# Revit family: IEK_R19_L2(2)_Шкаф_ЩМПп_IP66_TETRA_Навесной
name_source: partatom
category: Электрооборудование
units: mm (PartAtom-declared; Revit-internal decimal feet)

## family parameters
Всегда вертикально = Да
На основе рабочей плоскости = Нет
Общий = Нет
При загрузке вырезать с полостями = Нет
Размер круглого соединителя = Использовать диаметр
Тип детали = Силовой щит
Точка расчета площади = Да

## types (20) — shared parameters
ADSK_Версия Revit = 2019
ADSK_Версия семейства = v1.0 2023-02-20
ADSK_Группирование = Продукция НКУ
ADSK_Единица измерения = шт
ADSK_Завод-изготовитель = IEK
ADSK_Количество = 1
mS_Guid = 821c7fcf-6e20-4866-bf76-5fe537ee1ddb
Группировать в спецификации = Нет
Инженерная_сеть = Нет
Серия = TETRA
zero-valued in all types: mS_Координация оборудования

## per-type parameters (varying)
| type | ADSK_Код изделия | ADSK_Марка | ADSK_Масса | ADSK_Наименование | ADSK_Обозначение | ADSK_Размер_Высота | ADSK_Размер_Глубина | ADSK_Размер_Ширина |
| TETRA_ЩМПп_(310x210x140)_Пластик_Навесной_ПрозрДверь | TR5-11-N-030-20-13-65 | ЩМПп-310-210-140_IP66 | 1.31 | TETRA 5 Корпус пластик. ЩМПп 300х200х130мм прозр. IP66 IEK | ЩМПп-310-210-140_IP66 | 310 мм | 140 мм | 210 мм |
| TETRA_ЩМПп_(360x260x160)_Пластик_Навесной_ПрозрДверь | TR5-11-N-035-25-15-65 | ЩМПп-360-260-160_IP66 | 1.92 | TETRA 5 Корпус пластик. ЩМПп 350х250х150мм прозр. IP66 IEK | ЩМПп-360-260-160_IP66 | 360 мм | 160 мм | 260 мм |
| TETRA_ЩМПп_(410x310x180)_Пластик_Навесной_ПрозрДверь | TR5-11-N-040-30-17-65 | ЩМПп-410-310-180_IP66 | 3.373 | TETRA 5 Корпус пластик. ЩМПп 400х300х170мм прозр. IP66 IEK | ЩМПп-410-310-180_IP66 | 410 мм | 180 мм | 310 мм |
| TETRA_ЩМПп_(410x310x230)_Пластик_Навесной_ПрозрДверь | TR5-11-N-040-30-22-65 | ЩМПп-410-310-230_IP66 | 2.92 | TETRA 5 Корпус пластик. ЩМПп 400х300х220мм прозр. IP66 IEK | ЩМПп-410-310-230_IP66 | 410 мм | 230 мм | 310 мм |
| TETRA_ЩМПп_(510x360x200)_Пластик_Навесной_ПрозрДверь | TR5-11-N-050-35-19-65 | ЩМПп-510-360-200_IP66 | 3.9 | TETRA 5 Корпус пластик. ЩМПп 500х350х190мм прозр. IP66 IEK | ЩМПп-510-360-200_IP66 | 510 мм | 200 мм | 360 мм |
| TETRA_ЩМПп_(510x410x190)_Пластик_Навесной_ПрозрДверь | TR5-11-N-050-40-18-65 | ЩМПп-510-410-190_IP66 | 4.17 | TETRA 5 Корпус пластик. ЩМПп 500х400х180мм прозр. IP66 IEK | ЩМПп-510-410-190_IP66 | 510 мм | 190 мм | 410 мм |
| TETRA_ЩМПп_(510x410x250)_Пластик_Навесной_ПрозрДверь | TR5-11-N-050-40-24-65 | ЩМПп-510-410-250_IP66 | 4.77 | TETRA 5 Корпус пластик. ЩМПп 500х400х240мм прозр. IP66 IEK | ЩМПп-510-410-250_IP66 | 510 мм | 250 мм | 410 мм |
| TETRA_ЩМПп_(610x410x210)_Пластик_Навесной_ПрозрДверь | TR5-11-N-060-40-20-65 | ЩМПп-610-410-210_IP66 | 5.43 | TETRA 5 Корпус пластик. ЩМПп 600х400х200мм прозр. IP66 IEK | ЩМПп-610-410-210_IP66 | 610 мм | 210 мм | 410 мм |
| TETRA_ЩМПп_(710x510x260)_Пластик_Навесной_ПрозрДверь | TR5-11-N-070-50-25-65 | ЩМПп-710-510-260_IP66 | 8.1 | TETRA 5 Корпус пластик. ЩМПп 700х500х250мм прозр. IP66 IEK | ЩМПп-710-510-260_IP66 | 710 мм | 260 мм | 510 мм |
| TETRA_ЩМПп_(810x610x270)_Пластик_Навесной_ПрозрДверь | TR5-11-N-080-60-26-65 | ЩМПп-810-610-270_IP66 | 10.1 | TETRA 5 Корпус пластик. ЩМПп 800х600х260мм прозр. IP66 IEK | ЩМПп-810-610-270_IP66 | 810 мм | 270 мм | 610 мм |
| TETRA_ЩМПп_(310x210x140)_Пластик_Навесной | TR5-12-N-030-20-13-65 | ЩМПп-310-210-140_IP66 | 1.35 | TETRA 5 Корпус пластик. ЩМПп 300х200х130мм IP66 IEK | ЩМПп-310-210-140_IP66 | 310 мм | 140 мм | 210 мм |
| TETRA_ЩМПп_(360x260x160)_Пластик_Навесной | TR5-12-N-035-25-15-65 | ЩМПп-360-260-160_IP66 | 1.95 | TETRA 5 Корпус пластик. ЩМПп 350х250х150мм IP66 IEK | ЩМПп-360-260-160_IP66 | 360 мм | 160 мм | 260 мм |
| TETRA_ЩМПп_(410x310x180)_Пластик_Навесной | TR5-12-N-040-30-17-65 | ЩМПп-410-310-180_IP66 | 3.273 | TETRA 5 Корпус пластик. ЩМПп 400х300х170мм IP66 IEK | ЩМПп-410-310-180_IP66 | 410 мм | 180 мм | 310 мм |
| TETRA_ЩМПп_(410x310x230)_Пластик_Навесной | TR5-12-N-040-30-22-65 | ЩМПп-410-310-230_IP66 | 2.99 | TETRA 5 Корпус пластик. ЩМПп 400х300х220мм IP66 IEK | ЩМПп-410-310-230_IP66 | 410 мм | 230 мм | 310 мм |
| TETRA_ЩМПп_(510x360x200)_Пластик_Навесной | TR5-12-N-050-35-19-65 | ЩМПп-510-360-200_IP66 | 3.92 | TETRA 5 Корпус пластик. ЩМПп 500х350х190мм IP66 IEK | ЩМПп-510-360-200_IP66 | 510 мм | 200 мм | 360 мм |
| TETRA_ЩМПп_(510x410x190)_Пластик_Навесной | TR5-12-N-050-40-18-65 | ЩМПп-510-410-190_IP66 | 4.19 | TETRA 5 Корпус пластик. ЩМПп 500х400х180мм IP66 IEK | ЩМПп-510-410-190_IP66 | 510 мм | 190 мм | 410 мм |
| TETRA_ЩМПп_(510x410x250)_Пластик_Навесной | TR5-12-N-050-40-24-65 | ЩМПп-510-410-250_IP66 | 4.65 | TETRA 5 Корпус пластик. ЩМПп 500х400х240мм IP66 IEK | ЩМПп-510-410-250_IP66 | 510 мм | 250 мм | 410 мм |
| TETRA_ЩМПп_(610x410x210)_Пластик_Навесной | TR5-12-N-060-40-20-65 | ЩМПп-610-410-210_IP66 | 5.27 | TETRA 5 Корпус пластик. ЩМПп 600х400х200мм IP66 IEK | ЩМПп-610-410-210_IP66 | 610 мм | 210 мм | 410 мм |
| TETRA_ЩМПп_(710x510x260)_Пластик_Навесной | TR5-12-N-070-50-25-65 | ЩМПп-710-510-260_IP66 | 8 | TETRA 5 Корпус пластик. ЩМПп 700х500х250мм IP66 IEK | ЩМПп-710-510-260_IP66 | 710 мм | 260 мм | 510 мм |
| TETRA_ЩМПп_(810x610x270)_Пластик_Навесной | TR5-12-N-080-60-26-65 | ЩМПп-810-610-270_IP66 | 10.35 | TETRA 5 Корпус пластик. ЩМПп 800х600х260мм IP66 IEK | ЩМПп-810-610-270_IP66 | 810 мм | 270 мм | 610 мм |
